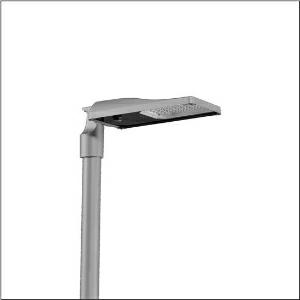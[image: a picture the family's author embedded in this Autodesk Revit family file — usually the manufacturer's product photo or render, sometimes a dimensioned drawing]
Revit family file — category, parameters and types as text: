
# Revit family: streetlight_sl_31_mini___st1_0a_5xh2d3ar08ha_7279
name_source: partatom
category: Lighting Fixtures
units: mm (PartAtom-declared; Revit-internal decimal feet)

## family parameters
Cut with Voids When Loaded = No
Host = Face
Light Source = No
Part Type = Normal
Room Calculation Point = No
Round Connector Dimension = Use Diameter
Shared = No

## types (1)
- --- (1 x LED, 9230 lm, 68.3 W, 3000K)
    Apparent Load = 68 VA
    CIE Flux Codes = 37 72 97 100 100
    Color Rendering = 70
    Color Temperature = 3000K
    Default Elevation = 1800 mm
    Description = Streetlight SL 31 mini D4i mast luminaire for post-top, side-entry; light control with lens of PMMA; light distribution: ST1.0a, direct asymmetric distribution, for standard-compliant lighting for roads and squares; LED: luminous flux: 9.230lm, light colour: 730, colour temperature: 3000K; luminous efficacy: 135,1lm/W; control: pre-setting: logarithmic dimming characteristic, flexible luminous flux parameterisation, time-dependent luminous flux control, constant luminous flux control, power reduction, intelligent temperature release in ECG and LED module, overheat protection; luminaire housing, of diecast aluminium, SITECO metallic grey (DB 702S), corrosivity category C5 high according to DIN EN ISO 12944; cover of toughened safety glass, transparent, mast flange of diecast aluminium, SITECO metallic grey (DB 702S), spigot size: 76/60mm, mast flange included unmounted; cable length: 8,5m, connection cable pre-assembled; mains connection: 220..240V, AC, 50/60Hz; power consumption (at start of service life): 68,3W / (at end of service life): 74,5W / (with reduced operation 50%): 29,5W; protection rating (complete): IP66; insulation class (complete): insulation class II (safety insulation); impact resistance: IK09; certification: CE, ENEC, ENEC+, VDE, UKCA, ZD4i; permissible operating ambient temperature for outdoor applications: -40..+50°C; packaging unit: 1 piece

Light Distribution: ST1.0a
    Height = 76 mm
    Lamp = 1 x LED
    Lamp Light Flux = 9230 lm
    Lamp Power = 68.3 W
    Lamp count = 1
    Length = 547 mm
    Luminous efficacy = 135 lm/W
    Manufacturer = Siteco
    ModVariant = No
    Model = 5XH2D3AR08HA
    Number of Poles = 1
    OnlyDefault = Yes
    Power Factor = 1
    Product Name = Streetlight SL 31 mini | ST1.0a
    Product group = mast luminaire | pylon top
    ProductGroupID = 6100
    Protection Class = Protection class II
    Protection Degree = IP 66
    RLX_Detail_Level = 1
    RLX_Emergency_Light_Flux = 0 lm
    RLX_Emergency_Type = 0
    RLX_Emergency_Type_DB = No
    RlxData = <blob elided: 39385 chars, md5=3cb1b6f0>
    Socket = socket
    Standby Power = 0 W
    System Light Flux = 9230 lm
    System Power = 68 W
    Type Comments = factory setting: luminous flux: 100 % | dim-lin: 254 | 692 mA
    Type Image = l_1300328.jpg
    URL = http://relux.com
    VarID = @adj_020701
    Voltage = 0 V
    Weight = 0.00 kg
    Width = 265 mm

## geometry (parser evidence)
native form markers: Blend x4, Sweep x9
no freeform markers — native parametric forms only
